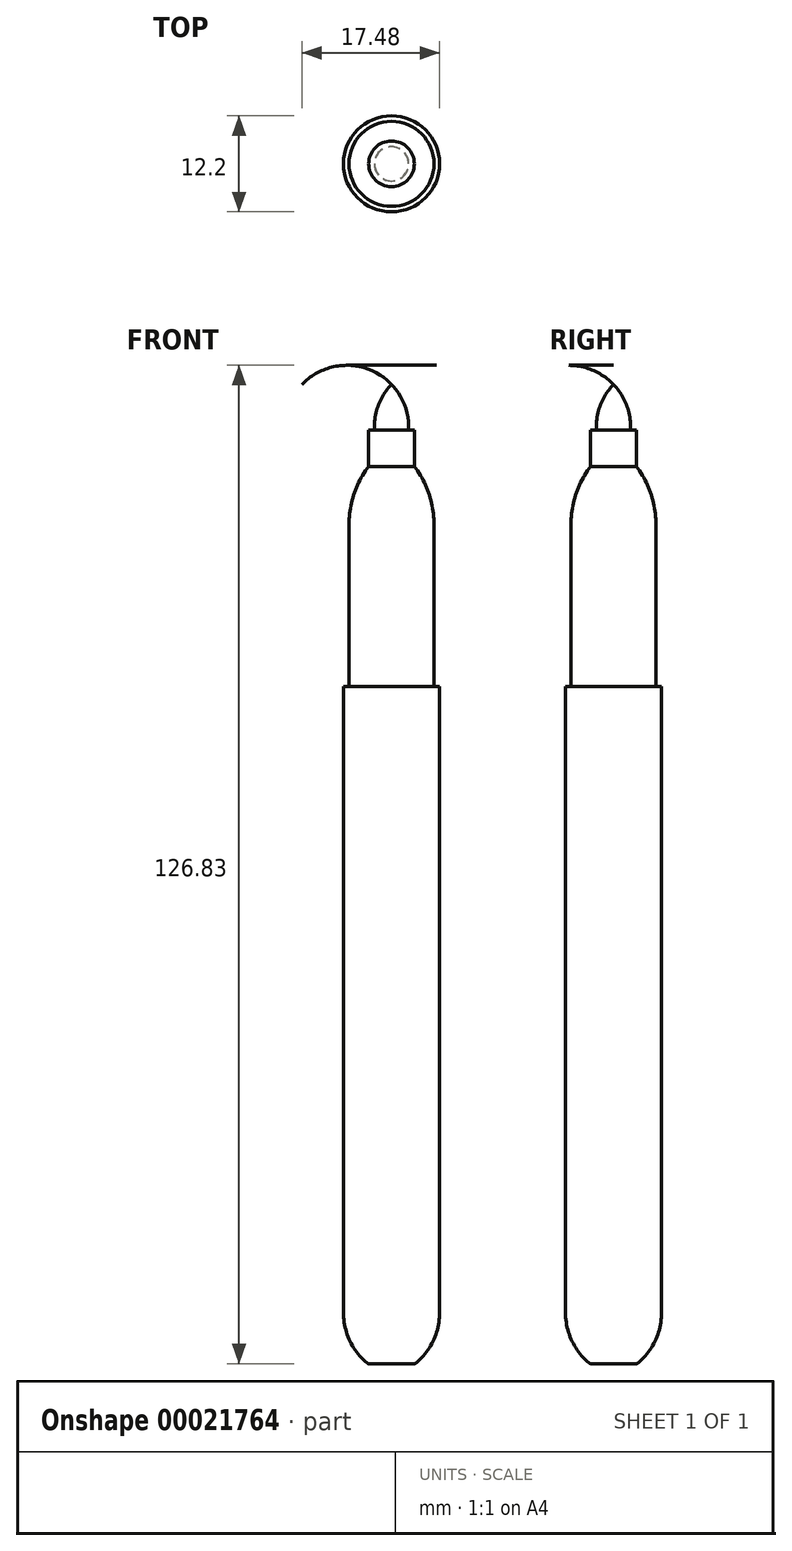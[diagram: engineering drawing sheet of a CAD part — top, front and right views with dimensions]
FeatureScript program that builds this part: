
annotation { "Feature Type Name" : "Feature", "Feature Type Description" : "" }
export const myFeature = defineFeature(function(context is Context, id is Id, definition is map)
    precondition{}
    {
        {
            var Q0;
            Q0=qCreatedBy(makeId("Front.planeOp"),FACE);
            var sketch = newSketch(context, id + "F0", { "sketchPlane" : qUnion([Q0])});
            skLineSegment(sketch, "E0", {"start": v(0, 0) * mm, "end": v(3, 0) * mm});
            skLineSegment(sketch, "E1", {"start": v(0, 0) * mm, "end": v(0, 6.5) * mm, "construction": true});
            skLineSegment(sketch, "E2", {"start": v(0, 6.5) * mm, "end": v(6.1, 6.5) * mm, "construction": true});
            skLineSegment(sketch, "E3", {"start": v(0, 0) * mm, "end": v(0, 1.45) * mm, "construction": true});
            skLineSegment(sketch, "E4", {"start": v(0, 0) * mm, "end": v(0, 86) * mm, "construction": true});
            skLineSegment(sketch, "E5", {"start": v(0, 86) * mm, "end": v(6.1, 86) * mm, "construction": true});
            skLineSegment(sketch, "E6", {"start": v(6.1, 86) * mm, "end": v(6.1, 6.5) * mm});
            skArc(sketch, "E7", {"start": v(6.1, 6.5) * mm, "mid": v(5.29, 2.9) * mm, "end": v(3, 0) * mm});
            skLineSegment(sketch, "E8", {"start": v(6.1, 86) * mm, "end": v(5.4, 86) * mm});
            skLineSegment(sketch, "E9", {"start": v(5.4, 86) * mm, "end": v(5.4, 106.6) * mm});
            skLineSegment(sketch, "E10", {"start": v(0, 86) * mm, "end": v(0, 114) * mm, "construction": true});
            skLineSegment(sketch, "E11", {"start": v(0, 114) * mm, "end": v(2.9, 114) * mm, "construction": true});
            skLineSegment(sketch, "E12", {"start": v(2.9, 114) * mm, "end": v(2.9, 118.6) * mm});
            skArc(sketch, "E13", {"start": v(5.4, 106.6) * mm, "mid": v(4.76, 110.5) * mm, "end": v(2.9, 114) * mm});
            skLineSegment(sketch, "E14", {"start": v(2.9, 118.6) * mm, "end": v(0, 118.6) * mm});
            skLineSegment(sketch, "E15", {"start": v(0, 118.6) * mm, "end": v(0, 0) * mm});
            skLineSegment(sketch, "E16", {"start": v(0, 86) * mm, "end": v(5.4, 86) * mm});
            skLineSegment(sketch, "E17", {"start": v(0, 118.6) * mm, "end": v(0, 124.4) * mm});
            skLineSegment(sketch, "E18", {"start": v(0, 118.6) * mm, "end": v(2.18, 118.6) * mm});
            skArc(sketch, "E19", {"start": v(2.18, 118.6) * mm, "mid": v(1.68, 121.72) * mm, "end": v(0, 124.4) * mm});
            skSolve(sketch);
        }
        {
            var Q0;
            Q0=makeQuery(id+"F0.imprint","IMPRINT",FACE,{"disambiguationData":[TD([[makeQuery(id+"F0.imprint","IMPRINT",EDGE,{"derivedFrom":sQuery(id+"F0.wireOp",EDGE,"E0")}),1.0]])]});
            var Q1;
            Q1=sQuery(id+"F0.wireOp",EDGE,"E15");
            revolve(context, id + "F1", {"entities" : qUnion([Q0]), "axis" : qUnion([Q1]), "revolveType" : RevolveType.FULL});
        }
        {
            var Q0;
            Q0=makeQuery(id+"F1.opRevolve","SWEPT_EDGE",EDGE,{"disambiguationData":[OSD([sQuery(id+"F0.wireOp",EDGE,"E0"),sQuery(id+"F0.wireOp",EDGE,"E7")])]});
            fillet(context, id + "F2", {"entities" : qUnion([Q0]), "radius" : .5 * mm, "tangentPropagation" : true, "allowEdgeOverflow" : false});
        }
        {
            var Q0;
            Q0=makeQuery(id+"F0.imprint","IMPRINT",FACE,{"disambiguationData":[TD([[makeQuery(id+"F0.imprint","IMPRINT",EDGE,{"derivedFrom":sQuery(id+"F0.wireOp",EDGE,"E9")}),1.0]])]});
            var Q1;
            Q1=sQuery(id+"F0.wireOp",EDGE,"E15");
            revolve(context, id + "F3", {"entities" : qUnion([Q0]), "axis" : qUnion([Q1]), "revolveType" : RevolveType.FULL});
        }
        {
            var Q0;
            Q0=makeQuery(id+"F0.imprint","IMPRINT",FACE,{"disambiguationData":[TD([[makeQuery(id+"F0.imprint","IMPRINT",EDGE,{"derivedFrom":sQuery(id+"F0.wireOp",EDGE,"E17")}),-1.0]])]});
            var Q1;
            Q1=sQuery(id+"F0.wireOp",EDGE,"E17");
            revolve(context, id + "F4", {"entities" : qUnion([Q0]), "axis" : qUnion([Q1]), "revolveType" : RevolveType.FULL});
        }
    });
